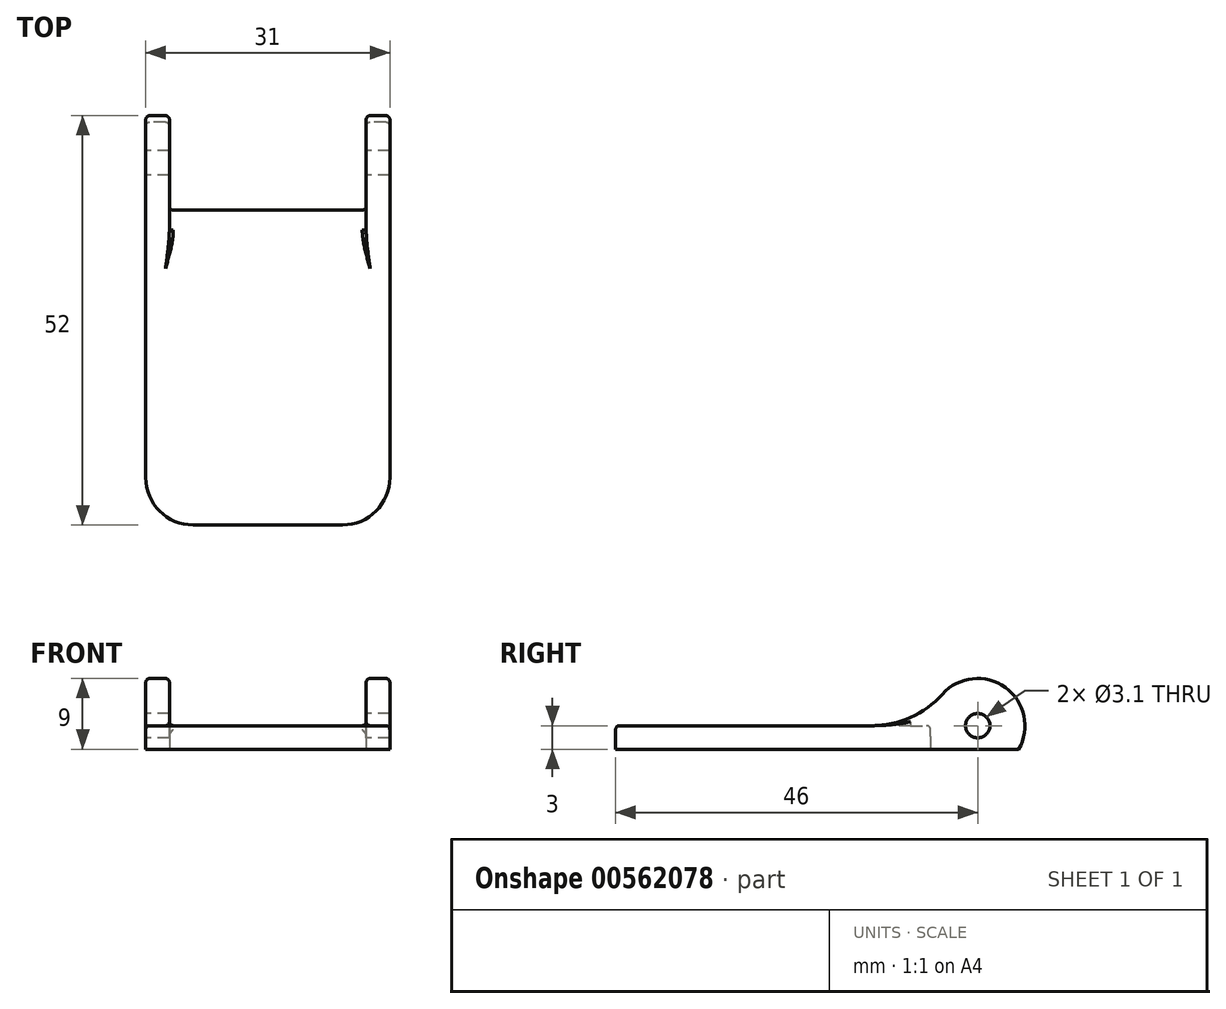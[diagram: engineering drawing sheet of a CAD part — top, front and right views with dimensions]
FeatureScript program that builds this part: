
annotation { "Feature Type Name" : "Feature", "Feature Type Description" : "" }
export const myFeature = defineFeature(function(context is Context, id is Id, definition is map)
    precondition{}
    {
        {
            var Q0;
            Q0=qCreatedBy(makeId("Right.planeOp"),FACE);
            var sketch = newSketch(context, id + "F0", { "sketchPlane" : qUnion([Q0])});
            skLineSegment(sketch, "E0", {"start": v(-46, 0) * mm, "end": v(5.2, 0) * mm});
            skLineSegment(sketch, "E1", {"start": v(-46, 0) * mm, "end": v(-46, 3) * mm});
            skLineSegment(sketch, "E2", {"start": v(-46, 3) * mm, "end": v(-6, 3) * mm});
            skArc(sketch, "E3", {"start": v(5.2, 0) * mm, "mid": v(1.55, 8.8) * mm, "end": v(-6, 3) * mm});
            skSolve(sketch);
        }
        {
            var Q0;
            Q0=makeQuery(id+"F0.imprint","IMPRINT",FACE,{"disambiguationData":[TD([[makeQuery(id+"F0.imprint","IMPRINT",EDGE,{"derivedFrom":sQuery(id+"F0.wireOp",EDGE,"E0")}),1.0]])]});
            extrude(context, id + "F1", {"entities" : qUnion([Q0]), "endBound" : BoundingType.SYMMETRIC, "depth" : 31 * mm, "offsetDistance" : 25 * mm});
        }
        {
            var Q0;
            Q0=makeQuery(id+"F1.opExtrude","SWEPT_FACE",FACE,{"disambiguationData":[OSD([sQuery(id+"F0.wireOp",EDGE,"E0")])]});
            var sketch = newSketch(context, id + "F2", { "sketchPlane" : qUnion([Q0])});
            skLineSegment(sketch, "E4.0", {"start": v(15.5, 6) * mm, "end": v(-15.5, 6) * mm});
            skLineSegment(sketch, "E5", {"start": v(12.5, -6) * mm, "end": v(-12.5, -6) * mm});
            skLineSegment(sketch, "E6", {"start": v(12.5, 6) * mm, "end": v(12.5, -6) * mm});
            skLineSegment(sketch, "E7", {"start": v(-12.5, 6) * mm, "end": v(-12.5, -6) * mm});
            skSolve(sketch);
        }
        {
            var Q0;
            Q0 = qSketchRegion(id + "F2", true);
            var Q1;
            Q1=makeQuery(id+"F1.opExtrude","SWEPT_BODY",BODY,{"disambiguationData":[OSD([sQuery(id+"F0.wireOp",EDGE,"E0"),sQuery(id+"F0.wireOp",EDGE,"E1"),sQuery(id+"F0.wireOp",EDGE,"E2"),sQuery(id+"F0.wireOp",EDGE,"E3")])]});
            extrude(context, id + "F3", {"entities" : qUnion([Q0]), "operationType" : NewBodyOperationType.REMOVE, "endBound" : BoundingType.UP_TO_BODY, "oppositeDirection" : true, "depth" : 25 * mm, "endBoundEntityBody" : qUnion([Q1]), "offsetDistance" : 25 * mm});
        }
        {
            var Q0;
            Q0=makeQuery(id+"F1.opExtrude","CAP_FACE",FACE,{"disambiguationData":[OSD([sQuery(id+"F0.wireOp",EDGE,"E0"),sQuery(id+"F0.wireOp",EDGE,"E1"),sQuery(id+"F0.wireOp",EDGE,"E2"),sQuery(id+"F0.wireOp",EDGE,"E3")])],"isStart":true});
            var sketch = newSketch(context, id + "F4", { "sketchPlane" : qUnion([Q0])});
            skArc(sketch, "E8.0", {"start": v(-5.2, 0) * mm, "mid": v(-1.55, 8.8) * mm, "end": v(6, 3) * mm, "construction": true});
            skCircle(sketch, "E9", {"center": v(0, 3) * mm, "radius": 1.55 * mm});
            skSolve(sketch);
        }
        {
            var Q0;
            Q0=makeQuery(id+"F4.imprint","IMPRINT",FACE,{"disambiguationData":[TD([[makeQuery(id+"F4.imprint","IMPRINT",EDGE,{"derivedFrom":sQuery(id+"F4.wireOp",EDGE,"E9")}),1.0]])]});
            var Q1;
            Q1=makeQuery(id+"F1.opExtrude","CAP_FACE",FACE,{"disambiguationData":[OSD([sQuery(id+"F0.wireOp",EDGE,"E0"),sQuery(id+"F0.wireOp",EDGE,"E1"),sQuery(id+"F0.wireOp",EDGE,"E2"),sQuery(id+"F0.wireOp",EDGE,"E3")])],"isStart":false});
            extrude(context, id + "F5", {"entities" : qUnion([Q0]), "operationType" : NewBodyOperationType.REMOVE, "endBound" : BoundingType.UP_TO_SURFACE, "oppositeDirection" : true, "depth" : 25 * mm, "endBoundEntityFace" : qUnion([Q1]), "offsetDistance" : 25 * mm});
        }
        {
            var Q0;
            {var subQ0=sQuery(id+"F0.wireOp",EDGE,"E3");var subQ1=sQuery(id+"F0.wireOp",EDGE,"E2");Q0=makeQuery(id+"F3.boolean.opBoolean","SPLIT",EDGE,{"disambiguationData":[TD([makeQuery(id+"F3.opExtrude","SWEPT_FACE",FACE,{"disambiguationData":[OSD([sQuery(id+"F2.wireOp",EDGE,"E7")])]})])],"derivedFrom":makeQuery(id+"F1.opExtrude","SWEPT_EDGE",EDGE,{"disambiguationData":[OSD([subQ1,subQ0])]})});}
            var Q1;
            {var subQ0=sQuery(id+"F0.wireOp",EDGE,"E3");var subQ1=sQuery(id+"F0.wireOp",EDGE,"E2");Q1=makeQuery(id+"F3.boolean.opBoolean","SPLIT",EDGE,{"disambiguationData":[TD([makeQuery(id+"F3.opExtrude","SWEPT_FACE",FACE,{"disambiguationData":[OSD([sQuery(id+"F2.wireOp",EDGE,"E6")])]})])],"derivedFrom":makeQuery(id+"F1.opExtrude","SWEPT_EDGE",EDGE,{"disambiguationData":[OSD([subQ1,subQ0])]})});}
            fillet(context, id + "F6", {"entities" : qUnion([Q0, Q1]), "radius" : 12 * mm, "tangentPropagation" : true, "allowEdgeOverflow" : false});
        }
        {
            var Q0;
            Q0=makeQuery(id+"F1.opExtrude","CAP_EDGE",EDGE,{"disambiguationData":[OSD([sQuery(id+"F0.wireOp",EDGE,"E1")])],"isStart":false});
            var Q1;
            Q1=makeQuery(id+"F1.opExtrude","CAP_EDGE",EDGE,{"disambiguationData":[OSD([sQuery(id+"F0.wireOp",EDGE,"E1")])],"isStart":true});
            fillet(context, id + "F7", {"entities" : qUnion([Q0, Q1]), "radius" : 6 * mm, "tangentPropagation" : true, "allowEdgeOverflow" : false});
        }
        {
            var Q0;
            Q0=makeQuery(id+"F1.opExtrude","CAP_EDGE",EDGE,{"disambiguationData":[OSD([sQuery(id+"F0.wireOp",EDGE,"E2")])],"isStart":true});
            var Q1;
            {var subQ0=makeQuery(id+"F3.opExtrude","SWEPT_FACE",FACE,{"disambiguationData":[OSD([sQuery(id+"F2.wireOp",EDGE,"E7")])]});var subQ1=sQuery(id+"F0.wireOp",EDGE,"E3");var subQ2=sQuery(id+"F0.wireOp",EDGE,"E2");Q1=makeQuery(id+"F6.opFillet","BLEND_EDGE",EDGE,{"blendedFrom":[makeQuery(id+"F3.boolean.opBoolean","SPLIT",EDGE,{"disambiguationData":[TD([subQ0])],"derivedFrom":makeQuery(id+"F1.opExtrude","SWEPT_EDGE",EDGE,{"disambiguationData":[OSD([subQ2,subQ1])]})}),makeQuery(id+"F3.boolean.opBoolean","COPY",FACE,{"derivedFrom":subQ0})],"blendedInto":[makeQuery(id+"F3.boolean.opBoolean","COPY",FACE,{"derivedFrom":subQ0})]});}
            var Q2;
            {var subQ0=makeQuery(id+"F3.opExtrude","SWEPT_FACE",FACE,{"disambiguationData":[OSD([sQuery(id+"F2.wireOp",EDGE,"E6")])]});var subQ1=sQuery(id+"F0.wireOp",EDGE,"E3");var subQ2=sQuery(id+"F0.wireOp",EDGE,"E2");Q2=makeQuery(id+"F6.opFillet","BLEND_EDGE",EDGE,{"blendedFrom":[makeQuery(id+"F3.boolean.opBoolean","SPLIT",EDGE,{"disambiguationData":[TD([subQ0])],"derivedFrom":makeQuery(id+"F1.opExtrude","SWEPT_EDGE",EDGE,{"disambiguationData":[OSD([subQ2,subQ1])]})}),makeQuery(id+"F3.boolean.opBoolean","COPY",FACE,{"derivedFrom":subQ0})],"blendedInto":[makeQuery(id+"F3.boolean.opBoolean","COPY",FACE,{"derivedFrom":subQ0})]});}
            var Q3;
            Q3=makeQuery(id+"F3.boolean.opBoolean","MERGE",EDGE,{"derivedFrom":[makeQuery(id+"F1.opExtrude","SWEPT_EDGE",EDGE,{"disambiguationData":[OSD([sQuery(id+"F0.wireOp",EDGE,"E2"),sQuery(id+"F0.wireOp",EDGE,"E3")])]})],"fromTools":[makeQuery(id+"F3.opExtrude","CAP_EDGE",EDGE,{"disambiguationData":[OSD([sQuery(id+"F2.wireOp",EDGE,"E4.0")])],"isStart":false})]});
            var Q4;
            Q4=makeQuery(id+"F6.opFillet","TWEAK_EDGE",EDGE,{"derivedFrom":[makeQuery(id+"F3.boolean.opBoolean","COPY",VERTEX,{"derivedFrom":makeQuery(id+"F3.opExtrude","CAP_VERTEX",VERTEX,{"disambiguationData":[OSD([sQuery(id+"F2.wireOp",EDGE,"E4.0"),sQuery(id+"F2.wireOp",EDGE,"E7")])],"isStart":false})})]});
            var Q5;
            Q5=makeQuery(id+"F6.opFillet","TWEAK_EDGE",EDGE,{"derivedFrom":[makeQuery(id+"F3.boolean.opBoolean","COPY",VERTEX,{"derivedFrom":makeQuery(id+"F3.opExtrude","CAP_VERTEX",VERTEX,{"disambiguationData":[OSD([sQuery(id+"F2.wireOp",EDGE,"E4.0"),sQuery(id+"F2.wireOp",EDGE,"E6")])],"isStart":false})})]});
            fillet(context, id + "F8", {"entities" : qUnion([Q0, Q1, Q2, Q3, Q4, Q5]), "radius" : 0.5 * mm, "tangentPropagation" : true, "allowEdgeOverflow" : false});
        }
    });
